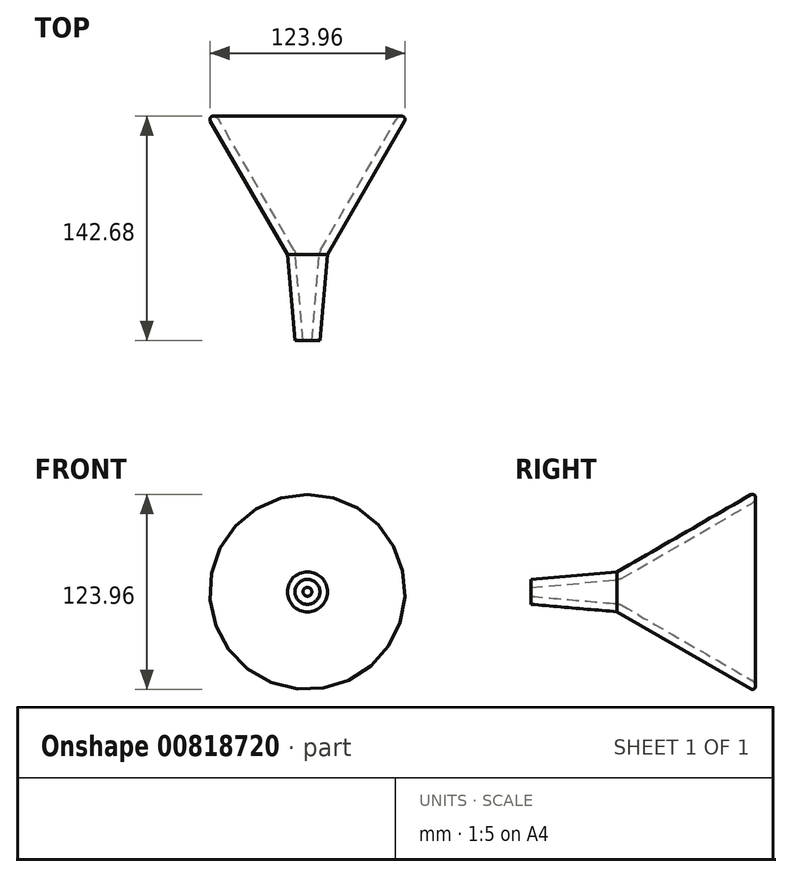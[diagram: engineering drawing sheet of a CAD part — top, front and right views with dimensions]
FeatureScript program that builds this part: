
annotation { "Feature Type Name" : "Feature", "Feature Type Description" : "" }
export const myFeature = defineFeature(function(context is Context, id is Id, definition is map)
    precondition{}
    {
        {
            var Q0;
            Q0=qCreatedBy(makeId("Top.planeOp"),FACE);
            var sketch = newSketch(context, id + "F0", { "sketchPlane" : qUnion([Q0])});
            skLineSegment(sketch, "E0", {"start": v(4.4, 90.62) * mm, "end": v(10.27, 90.62) * mm});
            skLineSegment(sketch, "E1", {"start": v(4.4, 90.62) * mm, "end": v(55.2, 2.63) * mm});
            skLineSegment(sketch, "E2", {"start": v(55.2, 2.63) * mm, "end": v(60, -52.13) * mm});
            skLineSegment(sketch, "E3.0", {"start": v(10.27, 90.62) * mm, "end": v(59.46, 5.41) * mm});
            skLineSegment(sketch, "E4.0", {"start": v(60.29, 2.8) * mm, "end": v(65.1, -52.13) * mm});
            skArc(sketch, "E5.filletArc", {"start": v(60.29, 2.8) * mm, "mid": v(60.02, 4.15) * mm, "end": v(59.46, 5.41) * mm});
            skLineSegment(sketch, "E6", {"start": v(60, -52.13) * mm, "end": v(65.1, -52.13) * mm});
            skLineSegment(sketch, "E7", {"start": v(67.9, -52.13) * mm, "end": v(67.9, 123.27) * mm, "construction": true});
            skSolve(sketch);
        }
        {
            var Q0;
            Q0=makeQuery(id+"F0.imprint","IMPRINT",FACE,{"disambiguationData":[TD([[makeQuery(id+"F0.imprint","IMPRINT",EDGE,{"derivedFrom":sQuery(id+"F0.wireOp",EDGE,"E0")}),-1.0]])]});
            var Q1;
            Q1=sQuery(id+"F0.wireOp",EDGE,"E7");
            revolve(context, id + "F1", {"surfaceOperationType" : NewSurfaceOperationType.NEW, "entities" : qUnion([Q0]), "axis" : qUnion([Q1]), "revolveType" : RevolveType.FULL});
        }
        {
            var Q0;
            Q0=makeQuery(id+"F1.opRevolve","SWEPT_FACE",FACE,{"disambiguationData":[OSD([sQuery(id+"F0.wireOp",EDGE,"E3.0")])]});
            var Q1;
            Q1=makeQuery(id+"F1.opRevolve","SWEPT_EDGE",EDGE,{"disambiguationData":[OSD([sQuery(id+"F0.wireOp",EDGE,"E0"),sQuery(id+"F0.wireOp",EDGE,"E3.0")])]});
            fillet(context, id + "F2", {"entities" : qUnion([Q0, Q1]), "radius" : 5.08 * mm, "tangentPropagation" : true, "allowEdgeOverflow" : false});
        }
        {
            var Q0;
            Q0=makeQuery(id+"F1.opRevolve","SWEPT_EDGE",EDGE,{"disambiguationData":[OSD([sQuery(id+"F0.wireOp",EDGE,"E0"),sQuery(id+"F0.wireOp",EDGE,"E1")])]});
            fillet(context, id + "F3", {"entities" : qUnion([Q0]), "radius" : 2.03 * mm, "tangentPropagation" : true, "allowEdgeOverflow" : false});
        }
    });
